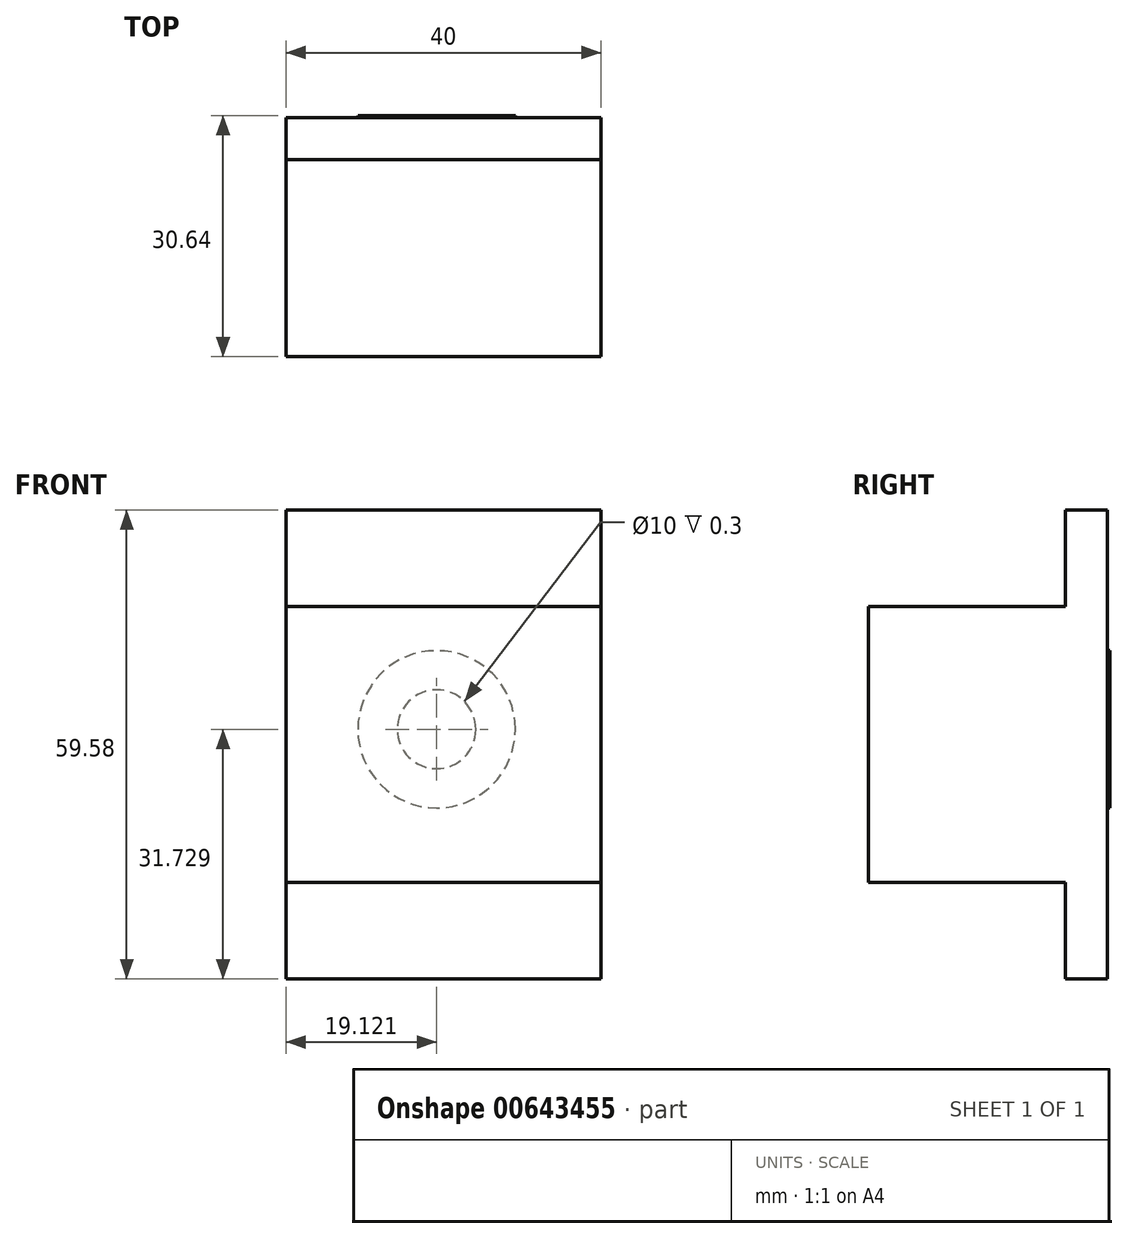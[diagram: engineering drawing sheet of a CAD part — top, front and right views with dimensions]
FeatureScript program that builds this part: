
annotation { "Feature Type Name" : "Feature", "Feature Type Description" : "" }
export const myFeature = defineFeature(function(context is Context, id is Id, definition is map)
    precondition{}
    {
        {
            var Q0;
            Q0=qCreatedBy(makeId("Right.planeOp"),FACE);
            var sketch = newSketch(context, id + "F0", { "sketchPlane" : qUnion([Q0])});
            skLineSegment(sketch, "E0.bottom", {"start": v(12.36, 11.2) * mm, "end": v(-12.64, 11.2) * mm});
            skLineSegment(sketch, "E0.top", {"start": v(12.36, -23.8) * mm, "end": v(-12.64, -23.8) * mm});
            skLineSegment(sketch, "E0.right", {"start": v(-12.64, 11.2) * mm, "end": v(-12.64, -23.8) * mm});
            skLineSegment(sketch, "E1.bottom", {"start": v(12.36, -36.12) * mm, "end": v(17.7, -36.12) * mm});
            skLineSegment(sketch, "E1.top", {"start": v(12.36, 23.46) * mm, "end": v(17.7, 23.46) * mm});
            skLineSegment(sketch, "E1.left", {"start": v(12.36, -36.12) * mm, "end": v(12.36, -23.8) * mm});
            skLineSegment(sketch, "E1.right", {"start": v(17.7, -36.12) * mm, "end": v(17.7, 23.46) * mm});
            skLineSegment(sketch, "E2.trimOffspring", {"start": v(12.36, 11.2) * mm, "end": v(12.36, 23.46) * mm});
            skSolve(sketch);
        }
        {
            var Q0;
            Q0 = qSketchRegion(id + "F0", true);
            extrude(context, id + "F1", {"entities" : qUnion([Q0]), "depth" : 40 * mm, "offsetDistance" : 25 * mm});
        }
        {
            var Q0;
            Q0=qCreatedBy(makeId("Front.planeOp"),FACE);
            var sketch = newSketch(context, id + "F2", { "sketchPlane" : qUnion([Q0])});
            skCircle(sketch, "E3", {"center": v(19.12, -4.4) * mm, "radius": 5 * mm});
            skCircle(sketch, "E4", {"center": v(19.12, -4.4) * mm, "radius": 10 * mm});
            skSolve(sketch);
        }
        {
            var Q0;
            Q0 = qSketchRegion(id + "F2", true);
            var Q1;
            Q1=makeQuery(id+"F1.opExtrude","SWEPT_FACE",FACE,{"disambiguationData":[OSD([sQuery(id+"F0.wireOp",EDGE,"E0.right")])]});
            extrude(context, id + "F3", {"entities" : qUnion([Q0, Q1]), "operationType" : NewBodyOperationType.ADD, "oppositeDirection" : true, "depth" : 18 * mm, "offsetDistance" : 25 * mm});
        }
    });
